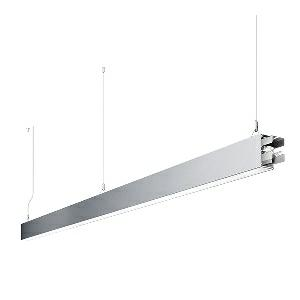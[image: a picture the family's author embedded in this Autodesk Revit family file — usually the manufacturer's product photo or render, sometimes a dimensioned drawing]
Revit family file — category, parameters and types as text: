
# Revit family: idoo_line_-_ilp_6000_830_d_sta_00805748_cacf
name_source: partatom
category: Lighting Fixtures
units: mm (PartAtom-declared; Revit-internal decimal feet)

## family parameters
Cut with Voids When Loaded = No
Host = Face
Light Source = No
Part Type = Normal
Room Calculation Point = No
Round Connector Dimension = Use Diameter
Shared = No

## types (1)
- IDOO.line - ILP 6000/830/D STA (1 x LED, 6000 lm, 3000K)
    Apparent Load = 46 VA
    Approval mark = CE
    CIE Flux Codes = 66 91 98 40 100
    Color Rendering = 80-89
    Color Temperature = 3000K
    Control Gear = Electronic ballast
    Default Elevation = 1800 mm
    Description = ILP 6000/830/D|Suspended luminaire|light source: LED|connected load: 220-240 V, 50/60 Hz|Power consumption: approx. 46 W|standby: approx. 0,15|luminous flux: 6000 lm|luminous efficacy: 130 lm/W|light distribution: Direct/indirect|direct ratio: approx. 40 %|colour temperature: Warm white, ca. 3000 K|color rendering index (CRI): >= 80|chromaticity tolerance:  3 SDCM|System of protection: IP 40|technology: Continuously dimmable|luminaire body|material: Sectional aluminium|colour: Silver|lamp cover: Acrylic (PMMA), Clear|mains lead: 2.00 m With free stranded wires|Fastening: Steel cable 0.3 - 0.7 m|glare control: Prism aperture|luminance(L65): <= 2700 cd/m|unified glare rating(4H 8H): <=  16|special features: DALI Load 1x, TouchDIM - dimming via standard switch, Through-wired, up to 18 m on one mains connection, Flicker-free, Suitable as emergency lighting, Start luminaire with mains connection, Mechanical and electrical connection of the individual modules without tools|
    Frequency = 50 Hz
    Height = 110 mm
    Lamp = 1 x LED
    Lamp Light Flux = 6000 lm
    Lamp count = 1
    Length = 2250 mm
    Luminous efficacy = 130 lm/W
    Manufacturer = Waldmann
    ModVariant = No
    Model = 00805748
    Mounting Place = Ceiling
    Mounting Type = Pendant
    Number of Poles = 1
    OnlyDefault = Yes
    Power Factor = 1
    Product Name = IDOO.line - ILP 6000/830/D STA
    Product group = Suspended luminaire
    ProductGroupID = 9
    Protection Class = Protection class I
    Protection Degree = IP 40
    RLX_Detail_Level = 1
    RLX_Emergency_Light_Flux = 0 lm
    RLX_Emergency_Type = 0
    RLX_Emergency_Type_DB = No
    RlxData = <blob elided: 24905 chars, md5=43c66991>
    Socket = socket
    Standby Power = 0 W
    System Light Flux = 6000 lm
    System Power = 46 W
    Type Comments = Product without accessories
    Type Image = 113316000-00692612.jpg
    URL = http://relux.com
    VarID = ---
    Voltage = 230 V
    Voltage Range = 220-240 V
    Weight = 0.00 kg
    Width = 60 mm  [stored 0.19685 ft]

note: [stored X ft] marks values corroborated as IEEE doubles in the binary element streams (Revit-internal decimal feet)

## geometry (parser evidence)
native form markers: Blend x4, Sweep x13
no freeform markers — native parametric forms only
